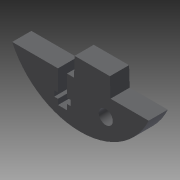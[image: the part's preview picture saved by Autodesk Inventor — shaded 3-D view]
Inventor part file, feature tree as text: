
AUTODESK INVENTOR PART (.ipt)
format: ipt  version: 2013 (Build 170138000, 138)  size: 157,696 bytes
history: native  units: mm
features: extrude x4, sketch x4, fillet x1
ambient origin geometry x8: Origin, YZ Plane, XZ Plane, XY Plane, X Axis, Y Axis, Z Axis, Center Point
bodies: Solid1 (feature_tree)
feature tree (9):
  extrude  "Extrusion1"  Depth=1.8mm
  fillet  "Fillet1"  Radius=1.8mm
  extrude  "Extrusion2"  Depth=1.25mm
  extrude  "Extrusion3"  Depth=25.0mm
  extrude  "Extrusion4"  Depth=5.0mm
  sketch  "Sketch1"  dims[d0=7.0mm d2=1.8mm d3=1.8mm]
  sketch  "Sketch2"  dims[d4=3.0mm d5=1.25mm]
  sketch  "Sketch3"  dims[d6=1.25mm d7=25.0mm]
  sketch  "Sketch4"  dims[d8=15.0mm d9=5.0mm d10=11.8mm d11=12.4mm d12=6.4mm d14=2.25mm d15=4.7mm d16=6.4mm d17=0.0mm d18=2.0mm d19=12.5mm d22=6.4mm d23=0.0mm d24=6.4mm d25=0.0mm d26=2.35mm d27=0.1mm d28=0.1mm d29=10.0mm d30=0.0mm]
